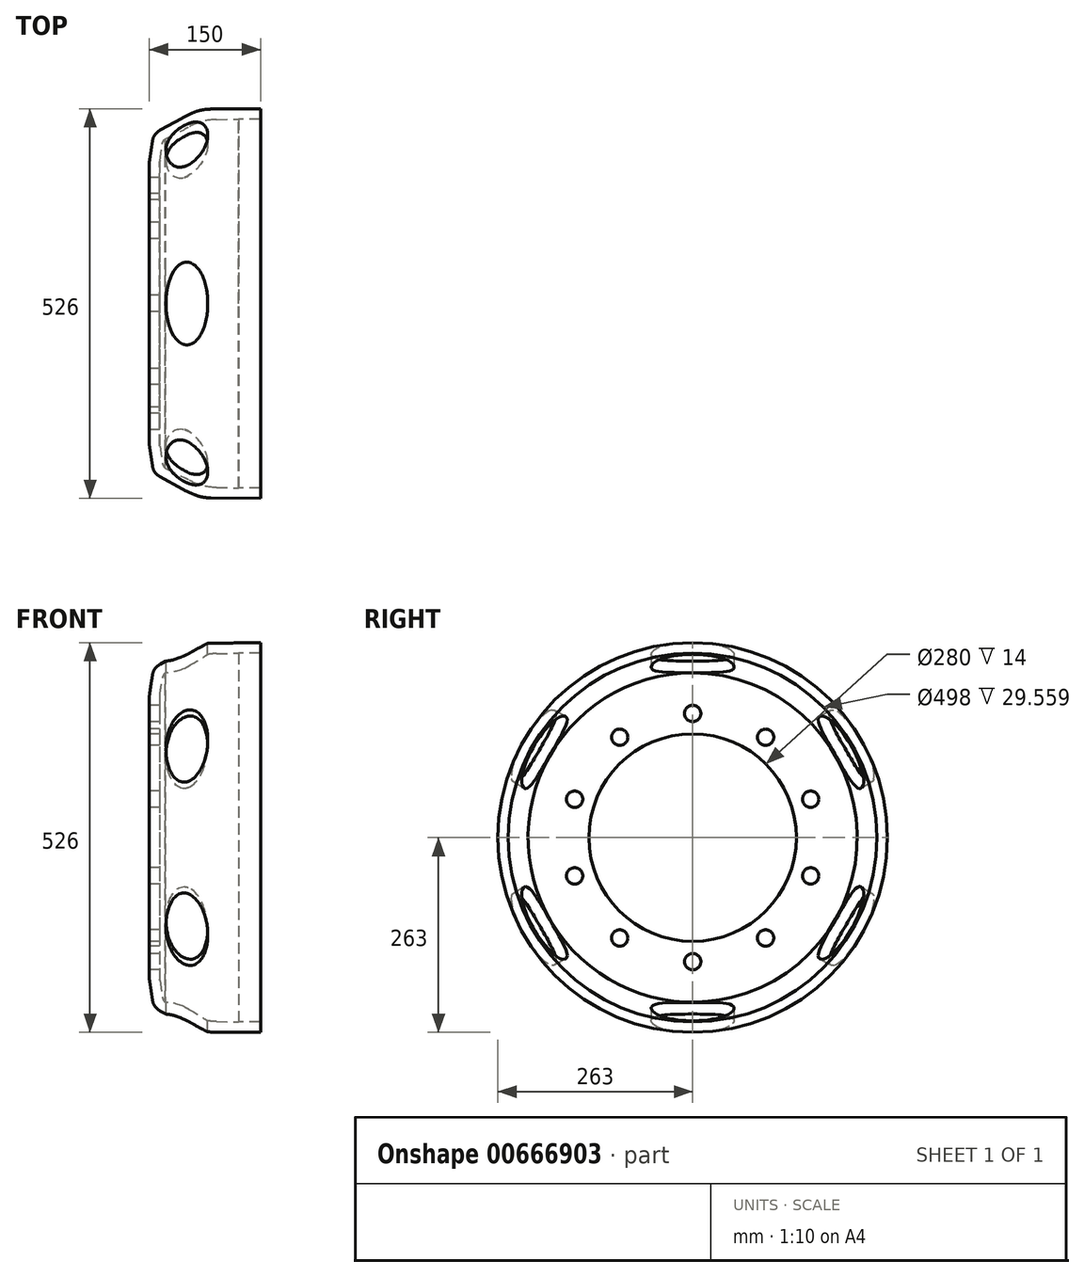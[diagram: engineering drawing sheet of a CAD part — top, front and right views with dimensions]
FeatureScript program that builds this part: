
annotation { "Feature Type Name" : "Feature", "Feature Type Description" : "" }
export const myFeature = defineFeature(function(context is Context, id is Id, definition is map)
    precondition{}
    {
        {
            var Q0;
            Q0=qCreatedBy(makeId("Front.planeOp"),FACE);
            var sketch = newSketch(context, id + "F0", { "sketchPlane" : qUnion([Q0])});
            skLineSegment(sketch, "E0", {"start": v(-248.74, 0) * mm, "end": v(278.06, 0) * mm, "construction": true});
            skLineSegment(sketch, "E1", {"start": v(0, 140) * mm, "end": v(-14, 140) * mm});
            skLineSegment(sketch, "E2", {"start": v(-14, 140) * mm, "end": v(-14, 189.76) * mm});
            skLineSegment(sketch, "E3", {"start": v(-13.67, 194.21) * mm, "end": v(-9.9, 219.31) * mm});
            skLineSegment(sketch, "E4", {"start": v(136, 263) * mm, "end": v(136, 249) * mm});
            skLineSegment(sketch, "E5", {"start": v(0, 140) * mm, "end": v(0, 191.4) * mm});
            skArc(sketch, "E6.filletArc", {"start": v(0.29, 233.9) * mm, "mid": v(-6.52, 227.8) * mm, "end": v(-9.9, 219.31) * mm});
            skPoint(sketch, "E7.visualSharp", {"position": v(-14, 192) * mm});
            skArc(sketch, "E7.filletArc", {"start": v(-13.67, 194.21) * mm, "mid": v(-13.92, 192) * mm, "end": v(-14, 189.76) * mm});
            skLineSegment(sketch, "E8", {"start": v(0.09, 192.6) * mm, "end": v(3.55, 215.67) * mm});
            skLineSegment(sketch, "E9", {"start": v(0.29, 233.9) * mm, "end": v(30.32, 250.3) * mm});
            skLineSegment(sketch, "E10", {"start": v(33.54, 251.94) * mm, "end": v(43.75, 256.74) * mm});
            skLineSegment(sketch, "E11", {"start": v(68.8, 262.45) * mm, "end": v(136, 263) * mm});
            skLineSegment(sketch, "E12", {"start": v(136, 249) * mm, "end": v(106.44, 249) * mm});
            skLineSegment(sketch, "E13", {"start": v(106.44, 249) * mm, "end": v(76.53, 248.39) * mm});
            skPoint(sketch, "E14.visualSharp", {"position": v(31.9, 251.17) * mm});
            skArc(sketch, "E14.filletArc", {"start": v(33.54, 251.94) * mm, "mid": v(31.92, 251.14) * mm, "end": v(30.32, 250.3) * mm});
            skPoint(sketch, "E15.visualSharp", {"position": v(55.65, 262.34) * mm});
            skArc(sketch, "E15.filletArc", {"start": v(68.8, 262.45) * mm, "mid": v(55.97, 260.95) * mm, "end": v(43.75, 256.74) * mm});
            skPoint(sketch, "E16.visualSharp", {"position": v(53.3, 247.91) * mm});
            skArc(sketch, "E16.filletArc", {"start": v(76.53, 248.39) * mm, "mid": v(56.97, 245.55) * mm, "end": v(38.71, 238) * mm});
            skPoint(sketch, "E17.visualSharp", {"position": v(0, 192) * mm});
            skArc(sketch, "E17.filletArc", {"start": v(0.09, 192.6) * mm, "mid": v(0.02, 192) * mm, "end": v(0, 191.4) * mm});
            skPoint(sketch, "E18.visualSharp", {"position": v(1.82, 204.1) * mm});
            skArc(sketch, "E18.filletArc", {"start": v(7.42, 222.17) * mm, "mid": v(4.85, 219.3) * mm, "end": v(3.55, 215.67) * mm});
            skLineSegment(sketch, "E19", {"start": v(7.42, 222.17) * mm, "end": v(33.18, 235.05) * mm});
            skPoint(sketch, "E20.visualSharp", {"position": v(36.62, 236.77) * mm});
            skArc(sketch, "E20.filletArc", {"start": v(33.18, 235.05) * mm, "mid": v(35.97, 236.49) * mm, "end": v(38.71, 238) * mm});
            skSolve(sketch);
        }
        {
            var Q0;
            Q0=makeQuery(id+"F0.imprint","IMPRINT",FACE,{"disambiguationData":[TD([[makeQuery(id+"F0.imprint","IMPRINT",EDGE,{"derivedFrom":sQuery(id+"F0.wireOp",EDGE,"E1")}),-1.0]])]});
            var Q1;
            Q1=sQuery(id+"F0.wireOp",EDGE,"E0");
            revolve(context, id + "F1", {"entities" : qUnion([Q0]), "axis" : qUnion([Q1]), "revolveType" : RevolveType.FULL});
        }
        {
            var Q0;
            Q0=makeQuery(id+"F1.opRevolve","SWEPT_FACE",FACE,{"disambiguationData":[OSD([sQuery(id+"F0.wireOp",EDGE,"E2")])]});
            var sketch = newSketch(context, id + "F2", { "sketchPlane" : qUnion([Q0])});
            skCircle(sketch, "E21", {"center": v(0, 0) * mm, "radius": 167.5 * mm});
            skPoint(sketch, "E22", {"position": v(0, 167.5) * mm});
            skPoint(sketch, "E23.1.0", {"position": v(-98.45, 135.51) * mm});
            skPoint(sketch, "E23.2.0", {"position": v(-159.3, 51.76) * mm});
            skPoint(sketch, "E23.3.0", {"position": v(-159.3, -51.76) * mm});
            skPoint(sketch, "E23.4.0", {"position": v(-98.45, -135.51) * mm});
            skPoint(sketch, "E23.5.0", {"position": v(0, -167.5) * mm});
            skPoint(sketch, "E23.6.0", {"position": v(98.45, -135.51) * mm});
            skPoint(sketch, "E23.7.0", {"position": v(159.3, -51.76) * mm});
            skPoint(sketch, "E23.8.0", {"position": v(159.3, 51.76) * mm});
            skPoint(sketch, "E23.9.0", {"position": v(98.45, 135.51) * mm});
            skSolve(sketch);
        }
        {
            var Q0;
            Q0=sQuery(id+"F2.wireOp",VERTEX,"E22");
            var Q1;
            Q1=sQuery(id+"F2.wireOp",VERTEX,"E23.9.0");
            var Q2;
            Q2=sQuery(id+"F2.wireOp",VERTEX,"E23.8.0");
            var Q3;
            Q3=sQuery(id+"F2.wireOp",VERTEX,"E23.7.0");
            var Q4;
            Q4=sQuery(id+"F2.wireOp",VERTEX,"E23.6.0");
            var Q5;
            Q5=sQuery(id+"F2.wireOp",VERTEX,"E23.5.0");
            var Q6;
            Q6=sQuery(id+"F2.wireOp",VERTEX,"E23.4.0");
            var Q7;
            Q7=sQuery(id+"F2.wireOp",VERTEX,"E23.3.0");
            var Q8;
            Q8=sQuery(id+"F2.wireOp",VERTEX,"E23.2.0");
            var Q9;
            Q9=sQuery(id+"F2.wireOp",VERTEX,"E23.1.0");
            var Q10;
            Q10=makeQuery(id+"F1.opRevolve","SWEPT_BODY",BODY,{"disambiguationData":[OSD([sQuery(id+"F0.wireOp",EDGE,"E1"),sQuery(id+"F0.wireOp",EDGE,"E2"),sQuery(id+"F0.wireOp",EDGE,"E3"),sQuery(id+"F0.wireOp",EDGE,"E4"),sQuery(id+"F0.wireOp",EDGE,"E5"),sQuery(id+"F0.wireOp",EDGE,"E6.filletArc"),sQuery(id+"F0.wireOp",EDGE,"E7.filletArc"),sQuery(id+"F0.wireOp",EDGE,"E8"),sQuery(id+"F0.wireOp",EDGE,"E9"),sQuery(id+"F0.wireOp",EDGE,"E10"),sQuery(id+"F0.wireOp",EDGE,"E11"),sQuery(id+"F0.wireOp",EDGE,"E12"),sQuery(id+"F0.wireOp",EDGE,"E13"),sQuery(id+"F0.wireOp",EDGE,"E14.filletArc"),sQuery(id+"F0.wireOp",EDGE,"E15.filletArc"),sQuery(id+"F0.wireOp",EDGE,"E16.filletArc"),sQuery(id+"F0.wireOp",EDGE,"E17.filletArc"),sQuery(id+"F0.wireOp",EDGE,"E18.filletArc"),sQuery(id+"F0.wireOp",EDGE,"E19"),sQuery(id+"F0.wireOp",EDGE,"E20.filletArc")])]});
            hole(context, id + "F3", {"style" : HoleStyle.SIMPLE, "endStyle" : HoleEndStyle.THROUGH, "standardTappedOrClearance" : lookupTablePath({ "standard" : "ISO", "size" : "22", "type" : "Drilled" }), "standardBlindInLast" : lookupTablePath({ "standard" : "ISO", "size" : "22", "type" : "Drilled" }), "holeDiameter" : 22 * mm, "majorDiameter" : 5 * mm, "tappedDepth" : 30 * mm, "tapClearance" : 3, "locations" : qUnion([Q0, Q1, Q2, Q3, Q4, Q5, Q6, Q7, Q8, Q9]), "scope" : qUnion([Q10])});
        }
        {
            var Q0;
            Q0 = qBodyType(qCreatedBy(id + "FYFfHytKsP5hBlq_1" ,EDGE), BodyType.WIRE);
            var Q1;
            Q1=qCreatedBy(makeId("Top.planeOp"),FACE);
            cPlane(context, id + "F4", {"entities" : qUnion([Q0, Q1]), "cplaneType" : CPlaneType.OFFSET, "offset" : (526 / 2) * mm, "width" : 150 * mm, "height" : 150 * mm});
        }
        {
            var Q0;
            Q0=qCreatedBy(id+"F4.planeOp",FACE);
            var sketch = newSketch(context, id + "F5", { "sketchPlane" : qUnion([Q0])});
            skEllipse(sketch, "E24", {"center": v(36.55, 0) * mm, "majorRadius": 55.86 * mm, "minorRadius": 28.22 * mm, "majorAxis": v(0, -1)});
            skSolve(sketch);
        }
        {
            var Q0;
            Q0=makeQuery(id+"F5.imprint","IMPRINT",FACE,{"disambiguationData":[TD([[makeQuery(id+"F5.imprint","IMPRINT",EDGE,{"derivedFrom":sQuery(id+"F5.wireOp",EDGE,"MBpKqVQN-SSv2-dmAW-gH3Q-B8E7CiTtgRoE")}),1.0]])]});
            var Q1;
            Q1=makeQuery(id+"F5.imprint","IMPRINT",FACE,{"disambiguationData":[TD([[makeQuery(id+"F5.imprint","IMPRINT",EDGE,{"derivedFrom":sQuery(id+"F5.wireOp",EDGE,"E24")}),1.0]])]});
            extrude(context, id + "F6", {"entities" : qUnion([Q0, Q1]), "operationType" : NewBodyOperationType.REMOVE, "oppositeDirection" : true, "depth" : 50 * mm, "offsetDistance" : 25 * mm});
        }
        {
            var Q0;
            Q0=makeQuery(id+"F6.boolean.opBoolean","COPY",FACE,{"derivedFrom":makeQuery(id+"F6.opExtrude","SWEPT_FACE",FACE,{"disambiguationData":[OSD([sQuery(id+"F5.wireOp",EDGE,"E24")])]})});
            var Q1;
            Q1=sQuery(id+"F0.wireOp",EDGE,"E0");
            circularPattern(context, id + "F7", {"patternType" : PatternType.FACE, "faces" : qUnion([Q0]), "axis" : qUnion([Q1]), "angle" : 360 * degree, "instanceCount" : 6, "equalSpace" : true});
        }
    });
